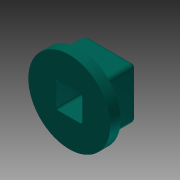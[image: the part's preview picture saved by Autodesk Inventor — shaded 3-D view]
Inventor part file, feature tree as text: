
AUTODESK INVENTOR PART (.ipt)
format: ipt  version: 2013 (Build 170138000, 138)  size: 129,536 bytes
history: native  units: in
note: dims shown in document units (in); Inventor stores cm internally (conversion verified against a paired STEP export)
features: extrude x4, sketch x4, fillet x2, other x1
ambient origin geometry x8: Origin, YZ Plane, XZ Plane, XY Plane, X Axis, Y Axis, Z Axis, Center Point
bodies: Solid1 (feature_tree)
feature tree (11):
  extrude  "Extrusion1"  Depth=0.05in TaperAngle=0.0deg
  extrude  "Extrusion2"  Depth=0.15in TaperAngle=0.0deg
  fillet  "Fillet1"  Radius=0.02in
  extrude  "Extrusion3"  Depth=1.0in TaperAngle=0.0deg
  fillet  "Fillet2"  Radius=0.01in
  sketch  "Sketch1"  dims[d0=0.395in d1=0.05in d2=0.0in]
  sketch  "Sketch2"  dims[d3=0.248in d4=0.15in d5=0.0in d6=0.02in]
  sketch  "Sketch4"  dims[d14=0.125in d15=1.0in d16=0.0in d17=0.01in]
  sketch  "Sketch5"  dims[d18=0.125in d19=0.0in d20=0.0in d21=0.0in]
  other  "Srf1"
  extrude  "ExtrusionSrf1"  TaperAngle=0.0deg  [1 undecoded]
note: 1 required parameter value undecoded (feature->parameter linkage not recoverable at this tier; creation-order binding heuristic only, values carry confidence <= 0.55)
